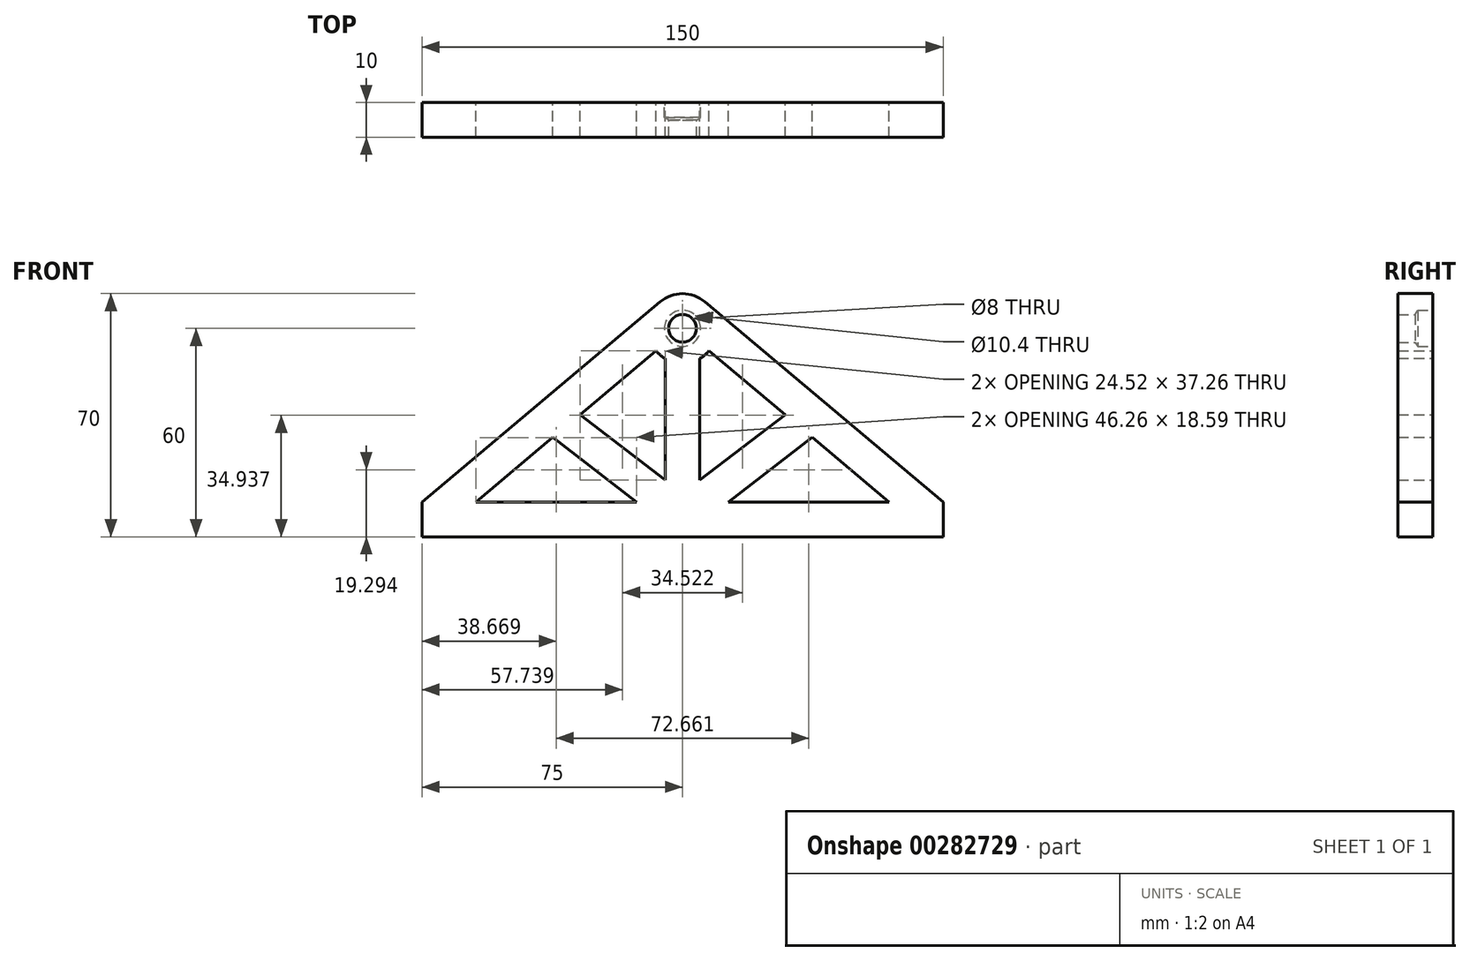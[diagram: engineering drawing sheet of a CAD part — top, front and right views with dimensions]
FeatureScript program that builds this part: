
annotation { "Feature Type Name" : "Feature", "Feature Type Description" : "" }
export const myFeature = defineFeature(function(context is Context, id is Id, definition is map)
    precondition{}
    {
        {
            var Q0;
            Q0=qCreatedBy(makeId("Front.planeOp"),FACE);
            var sketch = newSketch(context, id + "F0", { "sketchPlane" : qUnion([Q0])});
            skLineSegment(sketch, "E0.bottom", {"start": v(-75, 0) * mm, "end": v(75, 0) * mm});
            skLineSegment(sketch, "E0.left", {"start": v(-75, 0) * mm, "end": v(-75, 10) * mm});
            skLineSegment(sketch, "E0.right", {"start": v(75, 0) * mm, "end": v(75, 10) * mm});
            skLineSegment(sketch, "E1", {"start": v(0, 0) * mm, "end": v(0, 60) * mm, "construction": true});
            skPoint(sketch, "E2.orphan", {"position": v(-75, -6.19) * mm});
            skArc(sketch, "E3", {"start": v(-7.65, 53.56) * mm, "mid": v(-6.42, 52.34) * mm, "end": v(-5, 51.34) * mm});
            skLineSegment(sketch, "E4", {"start": v(-75, 10) * mm, "end": v(-6.44, 67.65) * mm});
            skLineSegment(sketch, "E5", {"start": v(-59.46, 10) * mm, "end": v(-37.36, 28.59) * mm});
            skLineSegment(sketch, "E6", {"start": v(-5, 51.34) * mm, "end": v(-5, 10) * mm});
            skLineSegment(sketch, "E7", {"start": v(-59.46, 10) * mm, "end": v(-13.2, 10) * mm});
            skLineSegment(sketch, "E8", {"start": v(-33.44, 31.88) * mm, "end": v(-5, 10) * mm, "construction": true});
            skPoint(sketch, "E9.trimOffspring.end.orphan", {"position": v(4.48, 63.76) * mm});
            skPoint(sketch, "E10.orphan", {"position": v(-71.35, 0) * mm});
            skLineSegment(sketch, "E11", {"start": v(-29.52, 35.18) * mm, "end": v(-5, 16.3) * mm});
            skLineSegment(sketch, "E12", {"start": v(-37.36, 28.59) * mm, "end": v(-13.2, 10) * mm});
            skArc(sketch, "E13.trimOffspring", {"start": v(5, 51.34) * mm, "mid": v(8.19, 65.74) * mm, "end": v(-6.44, 67.65) * mm});
            skLineSegment(sketch, "E14.trimOffspring", {"start": v(-29.52, 35.18) * mm, "end": v(-7.65, 53.56) * mm});
            skLineSegment(sketch, "E15.MirrorCS", {"start": v(75, 10) * mm, "end": v(6.44, 67.65) * mm});
            skLineSegment(sketch, "E16.MirrorCS", {"start": v(29.52, 35.18) * mm, "end": v(7.65, 53.56) * mm});
            skLineSegment(sketch, "E17.MirrorCS", {"start": v(5, 51.34) * mm, "end": v(5, 16.3) * mm});
            skLineSegment(sketch, "E18.MirrorCS", {"start": v(29.52, 35.18) * mm, "end": v(5, 16.3) * mm});
            skLineSegment(sketch, "E19.MirrorCS", {"start": v(37.36, 28.59) * mm, "end": v(13.2, 10) * mm});
            skLineSegment(sketch, "E20.MirrorCS", {"start": v(59.46, 10) * mm, "end": v(13.2, 10) * mm});
            skLineSegment(sketch, "E21.MirrorCS", {"start": v(59.46, 10) * mm, "end": v(37.36, 28.59) * mm});
            skPoint(sketch, "E22.orphan", {"position": v(-0.34, 12.72) * mm});
            skPoint(sketch, "E23.orphan", {"position": v(0.34, 12.72) * mm});
            skPoint(sketch, "E24.orphan", {"position": v(5, 10) * mm});
            skLineSegment(sketch, "E25.trimOffspring", {"start": v(13.2, 10) * mm, "end": v(75, 10) * mm});
            skSolve(sketch);
        }
        {
            var Q0;
            Q0=qSketchRegion(id+"F0",true);
            extrude(context, id + "F1", {"entities" : qUnion([Q0]), "depth" : 10 * mm});
        }
        {
            var Q0;
            Q0=sQuery(id+"F0.wireOp",VERTEX,"E3.center");
            var Q1;
            Q1=makeQuery(id+"F1.opExtrude","SWEPT_BODY",BODY,{"disambiguationData":[OSD([sQuery(id+"F0.wireOp",EDGE,"E0.bottom"),sQuery(id+"F0.wireOp",EDGE,"E0.left"),sQuery(id+"F0.wireOp",EDGE,"E0.right"),sQuery(id+"F0.wireOp",EDGE,"E3"),sQuery(id+"F0.wireOp",EDGE,"E4"),sQuery(id+"F0.wireOp",EDGE,"E5"),sQuery(id+"F0.wireOp",EDGE,"E6"),sQuery(id+"F0.wireOp",EDGE,"E7"),sQuery(id+"F0.wireOp",EDGE,"E11"),sQuery(id+"F0.wireOp",EDGE,"E12"),sQuery(id+"F0.wireOp",EDGE,"E13.trimOffspring"),sQuery(id+"F0.wireOp",EDGE,"E14.trimOffspring"),sQuery(id+"F0.wireOp",EDGE,"E15.MirrorCS"),sQuery(id+"F0.wireOp",EDGE,"E16.MirrorCS"),sQuery(id+"F0.wireOp",EDGE,"E17.MirrorCS"),sQuery(id+"F0.wireOp",EDGE,"E18.MirrorCS"),sQuery(id+"F0.wireOp",EDGE,"E19.MirrorCS"),sQuery(id+"F0.wireOp",EDGE,"E21.MirrorCS"),sQuery(id+"F0.wireOp",EDGE,"E25.trimOffspring")])]});
            hole(context, id + "F2", {"style" : HoleStyle.SIMPLE, "endStyle" : HoleEndStyle.BLIND, "oppositeDirection" : true, "holeDiameter" : 8 * mm, "holeDepth" : 25 * mm, "tappedDepth" : 12 * mm, "tapClearance" : 3, "locations" : qUnion([Q0]), "scope" : qUnion([Q1])});
        }
        {
            var Q0;
            Q0=sQuery(id+"F0.wireOp",VERTEX,"E3.center");
            var Q1;
            Q1=makeQuery(id+"F1.opExtrude","SWEPT_BODY",BODY,{"disambiguationData":[OSD([sQuery(id+"F0.wireOp",EDGE,"E0.bottom"),sQuery(id+"F0.wireOp",EDGE,"E0.left"),sQuery(id+"F0.wireOp",EDGE,"E0.right"),sQuery(id+"F0.wireOp",EDGE,"E3"),sQuery(id+"F0.wireOp",EDGE,"E4"),sQuery(id+"F0.wireOp",EDGE,"E5"),sQuery(id+"F0.wireOp",EDGE,"E6"),sQuery(id+"F0.wireOp",EDGE,"E7"),sQuery(id+"F0.wireOp",EDGE,"E11"),sQuery(id+"F0.wireOp",EDGE,"E12"),sQuery(id+"F0.wireOp",EDGE,"E13.trimOffspring"),sQuery(id+"F0.wireOp",EDGE,"E14.trimOffspring"),sQuery(id+"F0.wireOp",EDGE,"E15.MirrorCS"),sQuery(id+"F0.wireOp",EDGE,"E16.MirrorCS"),sQuery(id+"F0.wireOp",EDGE,"E17.MirrorCS"),sQuery(id+"F0.wireOp",EDGE,"E18.MirrorCS"),sQuery(id+"F0.wireOp",EDGE,"E19.MirrorCS"),sQuery(id+"F0.wireOp",EDGE,"E21.MirrorCS"),sQuery(id+"F0.wireOp",EDGE,"E25.trimOffspring")])]});
            hole(context, id + "F3", {"style" : HoleStyle.SIMPLE, "endStyle" : HoleEndStyle.BLIND, "oppositeDirection" : true, "holeDiameter" : 10.4 * mm, "holeDepth" : 4.3 * mm, "tappedDepth" : 12 * mm, "tapClearance" : 3, "locations" : qUnion([Q0]), "scope" : qUnion([Q1])});
        }
    });
